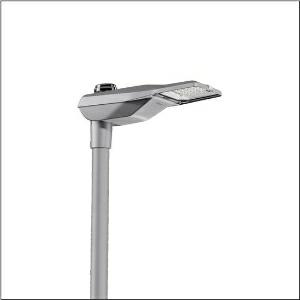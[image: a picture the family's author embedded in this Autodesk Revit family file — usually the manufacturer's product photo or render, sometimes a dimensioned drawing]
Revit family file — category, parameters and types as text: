
# Revit family: streetlight_sl_21_micro___st1_0a_5xe5d37n08db_4323
name_source: partatom
category: Lighting Fixtures
units: mm (PartAtom-declared; Revit-internal decimal feet)

## family parameters
Cut with Voids When Loaded = No
Host = Face
Light Source = No
Part Type = Normal
Room Calculation Point = No
Round Connector Dimension = Use Diameter
Shared = No

## types (1)
- --- (1 x LED, 5110 lm, 39.1 W, 3000K)
    Apparent Load = 39 VA
    CIE Flux Codes = 37 72 97 100 100
    Color Rendering = 70
    Color Temperature = 3000K
    Default Elevation = 1800 mm
    Description = Streetlight SL 21 micro, mast luminaire, primary light control with lens, of PMMA, primary optical cover: cover, of toughened safety glass, transparent, light distribution: ST1.0a, light emission: direct distribution, primary light characteristic: asymmetric, installation type: post-top, LED, 3G 1.5mm², High Power LED, rated luminous flux: 5.110lm, luminous efficacy: 131lm/W, light colour: 730, colour temperature: 3000K, control gear: NEMA (7pin), control: overheat protection, pre-setting: linear dimming characteristic, constant luminous flux control, time-dependent luminous flux control, flexible luminous flux parameterisation, mains connection: 230..240V, AC, 50/60Hz, connection cable pre-assembled, cable length: 6,5m, wiring characteristics: H07RN-F, start of lifetime: 39W, end of service life: 41W, reduction: 18W, luminaire housing, of diecast aluminium (EN AC-44300), powder-coated, Siteco® metallic grey (DB 702S), corrosivity category C5 mid according to DIN EN ISO 12944, multi-level sealing system, sealing non-destructively replaceable, inclination adjustable: 0°, 5°, 10°, 15°, length: 528mm, width: 235mm, height: 110mm, spigot size: 76/60mm (post-top), mounting height: 4..8m, protection rating (complete): IP66, insulation class (complete): insulation class I (protective earthing), certification: CE, ENEC, ENEC+, VDE, impact resistance: IK10, permissible operating ambient temperature for outdoor applications: -40..+50°C, standard-compliant lighting for roads and squares, packaging unit: 1 piece

Light Distribution: ST1.0a
    Height = 110 mm
    Lamp = 1 x LED
    Lamp Light Flux = 5110 lm
    Lamp Power = 39.1 W
    Lamp count = 1
    Length = 528 mm
    Luminous efficacy = 131 lm/W
    Manufacturer = Siteco
    ModVariant = No
    Model = 5XE5D37N08DB
    Number of Poles = 1
    OnlyDefault = Yes
    Power Factor = 1
    Product Name = Streetlight SL 21 micro | ST1.0a
    Product group = mast luminaire | pylon top
    ProductGroupID = 6100
    Protection Class = Protection class I
    Protection Degree = IP 66
    RLX_Detail_Level = 1
    RLX_Emergency_Light_Flux = 0 lm
    RLX_Emergency_Type = 0
    RLX_Emergency_Type_DB = No
    RlxData = <blob elided: 98841 chars, md5=b58a6f74>
    Socket = socket
    Standby Power = 0 W
    System Light Flux = 5110 lm
    System Power = 39 W
    Type Comments = factory setting: luminous flux: 100 % | dim-lin: 254 | 765 mA
    Type Image = l_1294375.jpg
    URL = http://relux.com
    VarID = @adj_158025
    Voltage = 0 V
    Weight = 0.00 kg
    Width = 235 mm

## geometry (parser evidence)
native form markers: Blend x4, Sweep x10
no freeform markers — native parametric forms only
